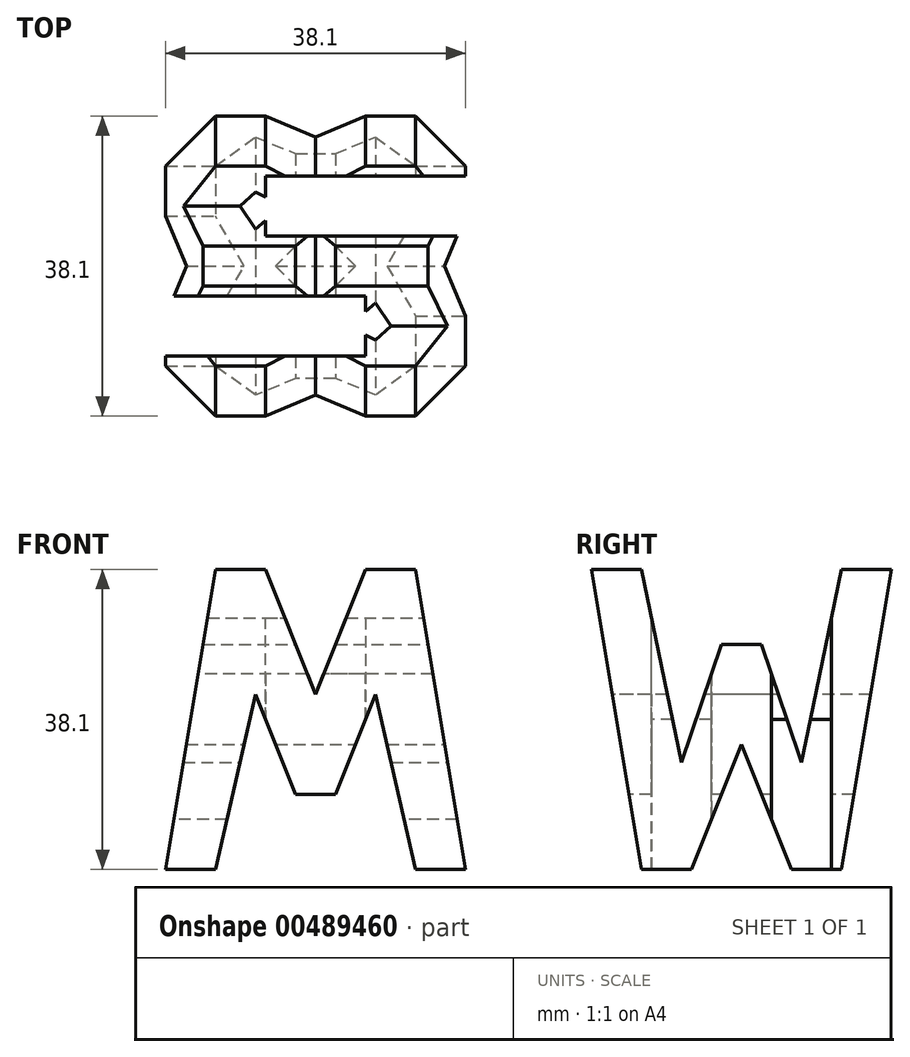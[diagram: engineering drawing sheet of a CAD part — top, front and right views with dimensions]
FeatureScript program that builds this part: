
annotation { "Feature Type Name" : "Feature", "Feature Type Description" : "" }
export const myFeature = defineFeature(function(context is Context, id is Id, definition is map)
    precondition{}
    {
        {
            var Q0;
            Q0=qCreatedBy(makeId("Front.planeOp"),FACE);
            var sketch = newSketch(context, id + "F0", { "sketchPlane" : qUnion([Q0])});
            skLineSegment(sketch, "E0", {"start": v(38.1, 0) * mm, "end": v(0, 0) * mm});
            skLineSegment(sketch, "E1", {"start": v(38.1, 0) * mm, "end": v(38.1, 38.1) * mm});
            skLineSegment(sketch, "E2", {"start": v(0, 38.1) * mm, "end": v(38.1, 38.1) * mm});
            skLineSegment(sketch, "E3", {"start": v(0, 38.1) * mm, "end": v(0, 0) * mm});
            skSolve(sketch);
        }
        {
            var Q0;
            Q0=makeQuery(id+"F0.imprint","IMPRINT",FACE,{"disambiguationData":[TD([[makeQuery(id+"F0.imprint","IMPRINT",EDGE,{"derivedFrom":sQuery(id+"F0.wireOp",EDGE,"E0")}),-1.0]])]});
            extrude(context, id + "F1", {"entities" : qUnion([Q0]), "depth" : 38.1 * mm, "offsetDistance" : 25.4 * mm});
        }
        {
            var Q0;
            Q0=qCreatedBy(makeId("Front.planeOp"),FACE);
            cPlane(context, id + "F2", {"entities" : qUnion([Q0]), "cplaneType" : CPlaneType.OFFSET, "offset" : 38.1 * mm, "width" : 152.4 * mm, "height" : 152.4 * mm});
        }
        {
            var Q0;
            Q0=qCreatedBy(makeId("Right.planeOp"),FACE);
            cPlane(context, id + "F3", {"entities" : qUnion([Q0]), "cplaneType" : CPlaneType.OFFSET, "offset" : 38.1 * mm, "width" : 152.4 * mm, "height" : 152.4 * mm});
        }
        {
            var Q0;
            Q0=qCreatedBy(makeId("Top.planeOp"),FACE);
            cPlane(context, id + "F4", {"entities" : qUnion([Q0]), "cplaneType" : CPlaneType.OFFSET, "offset" : 38.1 * mm, "width" : 152.4 * mm, "height" : 152.4 * mm});
        }
        {
            var Q0;
            Q0=qCreatedBy(id+"F3.planeOp",FACE);
            var sketch = newSketch(context, id + "F5", { "sketchPlane" : qUnion([Q0])});
            skLineSegment(sketch, "E4", {"start": v(0, 0) * mm, "end": v(-38.1, 0) * mm});
            skLineSegment(sketch, "E5", {"start": v(-38.1, 0) * mm, "end": v(-38.1, 38.1) * mm});
            skLineSegment(sketch, "E6", {"start": v(-38.1, 38.1) * mm, "end": v(0, 38.1) * mm});
            skLineSegment(sketch, "E7", {"start": v(0, 38.1) * mm, "end": v(0, 0) * mm});
            skLineSegment(sketch, "E8", {"start": v(-38.1, 38.1) * mm, "end": v(-31.75, 0) * mm});
            skLineSegment(sketch, "E9", {"start": v(-25.4, 0) * mm, "end": v(-19.05, 15.87) * mm});
            skLineSegment(sketch, "E10", {"start": v(-19.05, 15.87) * mm, "end": v(-12.7, 0) * mm});
            skLineSegment(sketch, "E11", {"start": v(-6.35, 0) * mm, "end": v(0, 38.1) * mm});
            skLineSegment(sketch, "E12", {"start": v(-31.75, 38.1) * mm, "end": v(-26.67, 13.57) * mm});
            skLineSegment(sketch, "E13", {"start": v(-26.67, 13.57) * mm, "end": v(-21.6, 28.57) * mm});
            skLineSegment(sketch, "E14", {"start": v(-21.59, 28.57) * mm, "end": v(-16.51, 28.57) * mm});
            skLineSegment(sketch, "E15", {"start": v(-16.51, 28.57) * mm, "end": v(-11.43, 13.57) * mm});
            skLineSegment(sketch, "E16", {"start": v(-11.43, 13.57) * mm, "end": v(-6.35, 38.1) * mm});
            skSolve(sketch);
        }
        {
            var Q0;
            {var subQ0=sQuery(id+"F5.wireOp",EDGE,"E12");Q0=makeQuery(id+"F5.imprint","IMPRINT",FACE,{"disambiguationData":[TD([[makeQuery(id+"F5.imprint","IMPRINT",EDGE,{"derivedFrom":subQ0}),1.0]])]});}
            var Q1;
            {var subQ0=sQuery(id+"F5.wireOp",EDGE,"E5");Q1=makeQuery(id+"F5.imprint","IMPRINT",FACE,{"disambiguationData":[TD([[makeQuery(id+"F5.imprint","IMPRINT",EDGE,{"derivedFrom":subQ0}),-1.0]])]});}
            var Q2;
            {var subQ0=sQuery(id+"F5.wireOp",EDGE,"E9");Q2=makeQuery(id+"F5.imprint","IMPRINT",FACE,{"disambiguationData":[TD([[makeQuery(id+"F5.imprint","IMPRINT",EDGE,{"derivedFrom":subQ0}),-1.0]])]});}
            var Q3;
            {var subQ0=sQuery(id+"F5.wireOp",EDGE,"E7");Q3=makeQuery(id+"F5.imprint","IMPRINT",FACE,{"disambiguationData":[TD([[makeQuery(id+"F5.imprint","IMPRINT",EDGE,{"derivedFrom":subQ0}),-1.0]])]});}
            extrude(context, id + "F6", {"entities" : qUnion([Q0, Q1, Q2, Q3]), "operationType" : NewBodyOperationType.REMOVE, "oppositeDirection" : true, "depth" : 38.1 * mm, "offsetDistance" : 25.4 * mm});
        }
        {
            var Q0;
            Q0=qCreatedBy(id+"F2.planeOp",FACE);
            var sketch = newSketch(context, id + "F7", { "sketchPlane" : qUnion([Q0])});
            skLineSegment(sketch, "E17", {"start": v(0, 0) * mm, "end": v(0, 38.1) * mm});
            skLineSegment(sketch, "E18", {"start": v(0, 38.1) * mm, "end": v(38.1, 38.1) * mm});
            skLineSegment(sketch, "E19", {"start": v(38.1, 38.1) * mm, "end": v(38.1, 0) * mm});
            skLineSegment(sketch, "E20", {"start": v(38.1, 0) * mm, "end": v(0, 0) * mm});
            skLineSegment(sketch, "E21", {"start": v(0, 0) * mm, "end": v(6.35, 38.1) * mm});
            skLineSegment(sketch, "E22", {"start": v(12.7, 38.1) * mm, "end": v(19.05, 22.22) * mm});
            skLineSegment(sketch, "E23", {"start": v(19.05, 22.22) * mm, "end": v(25.4, 38.1) * mm});
            skLineSegment(sketch, "E24", {"start": v(31.75, 38.1) * mm, "end": v(38.1, 0) * mm});
            skLineSegment(sketch, "E25", {"start": v(31.75, 0) * mm, "end": v(26.67, 22.23) * mm});
            skLineSegment(sketch, "E26", {"start": v(26.67, 22.23) * mm, "end": v(21.6, 9.52) * mm});
            skLineSegment(sketch, "E27", {"start": v(21.6, 9.52) * mm, "end": v(16.51, 9.52) * mm});
            skLineSegment(sketch, "E28", {"start": v(16.51, 9.52) * mm, "end": v(11.43, 22.23) * mm});
            skLineSegment(sketch, "E29", {"start": v(11.43, 22.23) * mm, "end": v(6.35, 0) * mm});
            skSolve(sketch);
        }
        {
            var Q0;
            {var subQ0=sQuery(id+"F7.wireOp",EDGE,"E22");Q0=makeQuery(id+"F7.imprint","IMPRINT",FACE,{"disambiguationData":[TD([[makeQuery(id+"F7.imprint","IMPRINT",EDGE,{"derivedFrom":subQ0}),1.0]])]});}
            var Q1;
            {var subQ0=sQuery(id+"F7.wireOp",EDGE,"E17");Q1=makeQuery(id+"F7.imprint","IMPRINT",FACE,{"disambiguationData":[TD([[makeQuery(id+"F7.imprint","IMPRINT",EDGE,{"derivedFrom":subQ0}),-1.0]])]});}
            var Q2;
            {var subQ0=sQuery(id+"F7.wireOp",EDGE,"E25");Q2=makeQuery(id+"F7.imprint","IMPRINT",FACE,{"disambiguationData":[TD([[makeQuery(id+"F7.imprint","IMPRINT",EDGE,{"derivedFrom":subQ0}),1.0]])]});}
            var Q3;
            {var subQ0=sQuery(id+"F7.wireOp",EDGE,"E19");Q3=makeQuery(id+"F7.imprint","IMPRINT",FACE,{"disambiguationData":[TD([[makeQuery(id+"F7.imprint","IMPRINT",EDGE,{"derivedFrom":subQ0}),-1.0]])]});}
            extrude(context, id + "F8", {"entities" : qUnion([Q0, Q1, Q2, Q3]), "operationType" : NewBodyOperationType.REMOVE, "oppositeDirection" : true, "depth" : 38.1 * mm, "offsetDistance" : 25.4 * mm});
        }
        {
            var Q0;
            Q0=qCreatedBy(id+"F4.planeOp",FACE);
            var sketch = newSketch(context, id + "F9", { "sketchPlane" : qUnion([Q0])});
            skLineSegment(sketch, "E30", {"start": v(0, 0) * mm, "end": v(0, -38.1) * mm});
            skLineSegment(sketch, "E31", {"start": v(0, -38.1) * mm, "end": v(38.1, -38.1) * mm});
            skLineSegment(sketch, "E32", {"start": v(38.1, -38.1) * mm, "end": v(38.1, 0) * mm});
            skLineSegment(sketch, "E33", {"start": v(38.1, 0) * mm, "end": v(0, 0) * mm});
            skLineSegment(sketch, "E34", {"start": v(0, -22.86) * mm, "end": v(25.4, -22.86) * mm});
            skLineSegment(sketch, "E35", {"start": v(25.4, -22.86) * mm, "end": v(25.4, -30.48) * mm});
            skLineSegment(sketch, "E36", {"start": v(25.4, -30.48) * mm, "end": v(0, -30.48) * mm});
            skLineSegment(sketch, "E37", {"start": v(38.1, -7.62) * mm, "end": v(12.7, -7.62) * mm});
            skLineSegment(sketch, "E38", {"start": v(12.7, -7.62) * mm, "end": v(12.7, -15.24) * mm});
            skLineSegment(sketch, "E39", {"start": v(12.7, -15.24) * mm, "end": v(38.1, -15.24) * mm});
            skSolve(sketch);
        }
        {
            var Q0;
            {var subQ0=sQuery(id+"F9.wireOp",EDGE,"E37");Q0=makeQuery(id+"F9.imprint","IMPRINT",FACE,{"disambiguationData":[TD([[makeQuery(id+"F9.imprint","IMPRINT",EDGE,{"derivedFrom":subQ0}),1.0]])]});}
            var Q1;
            {var subQ0=sQuery(id+"F9.wireOp",EDGE,"E34");Q1=makeQuery(id+"F9.imprint","IMPRINT",FACE,{"disambiguationData":[TD([[makeQuery(id+"F9.imprint","IMPRINT",EDGE,{"derivedFrom":subQ0}),-1.0]])]});}
            extrude(context, id + "F10", {"entities" : qUnion([Q0, Q1]), "operationType" : NewBodyOperationType.REMOVE, "oppositeDirection" : true, "depth" : 38.1 * mm, "offsetDistance" : 25.4 * mm});
        }
    });
